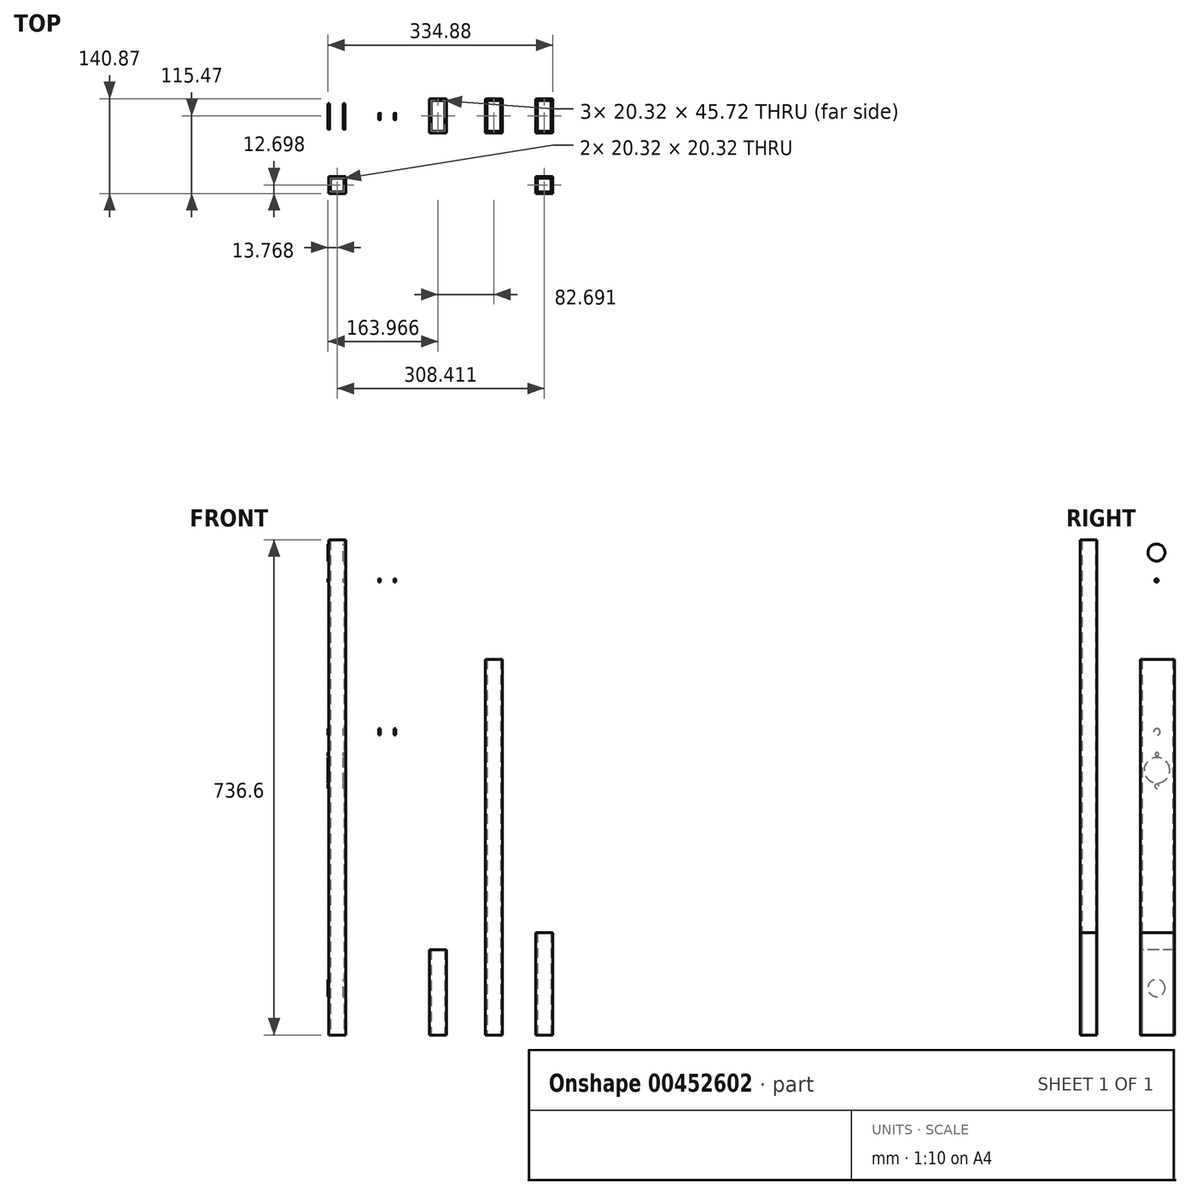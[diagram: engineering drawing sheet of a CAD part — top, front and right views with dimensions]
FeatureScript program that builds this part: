
annotation { "Feature Type Name" : "Feature", "Feature Type Description" : "" }
export const myFeature = defineFeature(function(context is Context, id is Id, definition is map)
    precondition{}
    {
        {
            var Q0;
            Q0=qCreatedBy(makeId("Top.planeOp"),FACE);
            var sketch = newSketch(context, id + "F0", { "sketchPlane" : qUnion([Q0])});
            skLineSegment(sketch, "E0.bottom", {"start": v(-12.7, 25.4) * mm, "end": v(12.7, 25.4) * mm});
            skLineSegment(sketch, "E0.top", {"start": v(-12.7, -25.4) * mm, "end": v(12.7, -25.4) * mm});
            skLineSegment(sketch, "E0.left", {"start": v(-12.7, 25.4) * mm, "end": v(-12.7, -25.4) * mm});
            skLineSegment(sketch, "E0.right", {"start": v(12.7, 25.4) * mm, "end": v(12.7, -25.4) * mm});
            skPoint(sketch, "E0.middle", {"position": v(0, 0) * mm});
            skLineSegment(sketch, "E1.0", {"start": v(-10.16, 22.86) * mm, "end": v(10.16, 22.86) * mm});
            skLineSegment(sketch, "E1.1", {"start": v(-10.16, 22.86) * mm, "end": v(-10.16, -22.86) * mm});
            skLineSegment(sketch, "E1.2", {"start": v(-10.16, -22.86) * mm, "end": v(10.16, -22.86) * mm});
            skLineSegment(sketch, "E1.3", {"start": v(10.16, 22.86) * mm, "end": v(10.16, -22.86) * mm});
            skLineSegment(sketch, "E2", {"start": v(37.87, 30.47) * mm, "end": v(37.87, -46.83) * mm, "construction": true});
            skLineSegment(sketch, "E3.MirrorCS", {"start": v(88.45, 25.4) * mm, "end": v(63.05, 25.4) * mm});
            skLineSegment(sketch, "E4.MirrorCS", {"start": v(88.45, -25.4) * mm, "end": v(63.05, -25.4) * mm});
            skLineSegment(sketch, "E5.MirrorCS", {"start": v(88.45, 25.4) * mm, "end": v(88.45, -25.4) * mm});
            skLineSegment(sketch, "E6.MirrorCS", {"start": v(63.05, 25.4) * mm, "end": v(63.05, -25.4) * mm});
            skPoint(sketch, "E7.MirrorP", {"position": v(75.75, 0) * mm});
            skLineSegment(sketch, "E8.MirrorCS", {"start": v(85.9, 22.86) * mm, "end": v(65.59, 22.86) * mm});
            skLineSegment(sketch, "E9.MirrorCS", {"start": v(85.9, 22.86) * mm, "end": v(85.9, -22.86) * mm});
            skLineSegment(sketch, "E10.MirrorCS", {"start": v(85.9, -22.86) * mm, "end": v(65.59, -22.86) * mm});
            skLineSegment(sketch, "E11.MirrorCS", {"start": v(65.59, 22.86) * mm, "end": v(65.59, -22.86) * mm});
            skLineSegment(sketch, "E12", {"start": v(113.5, 33.8) * mm, "end": v(113.5, -57.25) * mm, "construction": true});
            skPoint(sketch, "E13.MirrorP", {"position": v(151.27, 0) * mm});
            skLineSegment(sketch, "E14.MirrorCS", {"start": v(161.43, 22.86) * mm, "end": v(161.43, -22.86) * mm});
            skLineSegment(sketch, "E15.MirrorCS", {"start": v(163.97, 25.4) * mm, "end": v(163.97, -25.4) * mm});
            skLineSegment(sketch, "E16.MirrorCS", {"start": v(138.57, 25.4) * mm, "end": v(138.57, -25.4) * mm});
            skLineSegment(sketch, "E17.MirrorCS", {"start": v(138.57, -25.4) * mm, "end": v(163.97, -25.4) * mm});
            skLineSegment(sketch, "E18.MirrorCS", {"start": v(138.57, 25.4) * mm, "end": v(163.97, 25.4) * mm});
            skLineSegment(sketch, "E19.MirrorCS", {"start": v(141.1, 22.86) * mm, "end": v(161.43, 22.86) * mm});
            skLineSegment(sketch, "E20.MirrorCS", {"start": v(141.1, -22.86) * mm, "end": v(161.43, -22.86) * mm});
            skLineSegment(sketch, "E21.MirrorCS", {"start": v(141.1, 22.86) * mm, "end": v(141.1, -22.86) * mm});
            skLineSegment(sketch, "E22", {"start": v(192.61, 38.44) * mm, "end": v(192.61, -69.07) * mm, "construction": true});
            skLineSegment(sketch, "E23.MirrorCS", {"start": v(397.93, 25.4) * mm, "end": v(372.53, 25.4) * mm});
            skLineSegment(sketch, "E24.MirrorCS", {"start": v(397.93, -25.4) * mm, "end": v(372.53, -25.4) * mm});
            skLineSegment(sketch, "E25.MirrorCS", {"start": v(395.39, 22.86) * mm, "end": v(375.07, 22.86) * mm});
            skLineSegment(sketch, "E26.MirrorCS", {"start": v(395.39, -22.86) * mm, "end": v(375.07, -22.86) * mm});
            skLineSegment(sketch, "E27.MirrorCS", {"start": v(397.93, 25.4) * mm, "end": v(397.93, -25.4) * mm});
            skLineSegment(sketch, "E28.MirrorCS", {"start": v(395.39, 22.86) * mm, "end": v(395.39, -22.86) * mm});
            skLineSegment(sketch, "E29.MirrorCS", {"start": v(375.07, 22.86) * mm, "end": v(375.07, -22.86) * mm});
            skLineSegment(sketch, "E30.MirrorCS", {"start": v(299.32, 22.86) * mm, "end": v(319.64, 22.86) * mm});
            skLineSegment(sketch, "E31.MirrorCS", {"start": v(299.32, -22.86) * mm, "end": v(319.64, -22.86) * mm});
            skLineSegment(sketch, "E32.MirrorCS", {"start": v(246.66, 25.4) * mm, "end": v(246.66, -25.4) * mm});
            skLineSegment(sketch, "E33.MirrorCS", {"start": v(244.12, 22.86) * mm, "end": v(223.8, 22.86) * mm});
            skLineSegment(sketch, "E34.MirrorCS", {"start": v(244.12, -22.86) * mm, "end": v(223.8, -22.86) * mm});
            skLineSegment(sketch, "E35.MirrorCS", {"start": v(246.66, 25.4) * mm, "end": v(221.26, 25.4) * mm});
            skLineSegment(sketch, "E36.MirrorCS", {"start": v(296.78, 25.4) * mm, "end": v(322.18, 25.4) * mm});
            skLineSegment(sketch, "E37.MirrorCS", {"start": v(296.78, -25.4) * mm, "end": v(322.18, -25.4) * mm});
            skLineSegment(sketch, "E38.MirrorCS", {"start": v(246.66, -25.4) * mm, "end": v(221.26, -25.4) * mm});
            skLineSegment(sketch, "E39.MirrorCS", {"start": v(223.8, 22.86) * mm, "end": v(223.8, -22.86) * mm});
            skLineSegment(sketch, "E40.MirrorCS", {"start": v(299.32, 22.86) * mm, "end": v(299.32, -22.86) * mm});
            skLineSegment(sketch, "E41.MirrorCS", {"start": v(319.64, 22.86) * mm, "end": v(319.64, -22.86) * mm});
            skLineSegment(sketch, "E42.MirrorCS", {"start": v(372.53, 25.4) * mm, "end": v(372.53, -25.4) * mm});
            skPoint(sketch, "E43.MirrorP", {"position": v(385.23, 0) * mm});
            skLineSegment(sketch, "E44.MirrorCS", {"start": v(244.12, 22.86) * mm, "end": v(244.12, -22.86) * mm});
            skLineSegment(sketch, "E45.MirrorCS", {"start": v(221.26, 25.4) * mm, "end": v(221.26, -25.4) * mm});
            skLineSegment(sketch, "E46.MirrorCS", {"start": v(296.78, 25.4) * mm, "end": v(296.78, -25.4) * mm});
            skPoint(sketch, "E47.MirrorP", {"position": v(233.96, 0) * mm});
            skPoint(sketch, "E48.MirrorP", {"position": v(309.48, 0) * mm});
            skLineSegment(sketch, "E49.MirrorCS", {"start": v(271.72, 33.8) * mm, "end": v(271.72, -57.25) * mm, "construction": true});
            skLineSegment(sketch, "E50.MirrorCS", {"start": v(347.35, 30.47) * mm, "end": v(347.35, -46.83) * mm, "construction": true});
            skLineSegment(sketch, "E51.MirrorCS", {"start": v(322.18, 25.4) * mm, "end": v(322.18, -25.4) * mm});
            skLineSegment(sketch, "E52", {"start": v(-40.7, 40.51) * mm, "end": v(-40.7, -117.08) * mm, "construction": true});
            skLineSegment(sketch, "E53.MirrorCS", {"start": v(-479.32, 25.4) * mm, "end": v(-453.92, 25.4) * mm});
            skLineSegment(sketch, "E54.MirrorCS", {"start": v(-476.78, 22.86) * mm, "end": v(-456.46, 22.86) * mm});
            skLineSegment(sketch, "E55.MirrorCS", {"start": v(-479.32, -25.4) * mm, "end": v(-453.92, -25.4) * mm});
            skLineSegment(sketch, "E56.MirrorCS", {"start": v(-68.7, -25.4) * mm, "end": v(-94.1, -25.4) * mm});
            skLineSegment(sketch, "E57.MirrorCS", {"start": v(-453.92, 25.4) * mm, "end": v(-453.92, -25.4) * mm});
            skLineSegment(sketch, "E58.MirrorCS", {"start": v(-68.7, 25.4) * mm, "end": v(-94.1, 25.4) * mm});
            skLineSegment(sketch, "E59.MirrorCS", {"start": v(-71.23, -22.86) * mm, "end": v(-91.55, -22.86) * mm});
            skLineSegment(sketch, "E60.MirrorCS", {"start": v(-476.78, -22.86) * mm, "end": v(-456.46, -22.86) * mm});
            skLineSegment(sketch, "E61.MirrorCS", {"start": v(-71.23, 22.86) * mm, "end": v(-91.55, 22.86) * mm});
            skLineSegment(sketch, "E62.MirrorCS", {"start": v(-456.46, 22.86) * mm, "end": v(-456.46, -22.86) * mm});
            skLineSegment(sketch, "E63.MirrorCS", {"start": v(-68.7, 25.4) * mm, "end": v(-68.7, -25.4) * mm});
            skLineSegment(sketch, "E64.MirrorCS", {"start": v(-479.32, 25.4) * mm, "end": v(-479.32, -25.4) * mm});
            skLineSegment(sketch, "E65.MirrorCS", {"start": v(-328.05, 25.4) * mm, "end": v(-302.65, 25.4) * mm});
            skLineSegment(sketch, "E66.MirrorCS", {"start": v(-476.78, 22.86) * mm, "end": v(-476.78, -22.86) * mm});
            skLineSegment(sketch, "E67.MirrorCS", {"start": v(-219.96, 25.4) * mm, "end": v(-245.36, 25.4) * mm});
            skLineSegment(sketch, "E68.MirrorCS", {"start": v(-325.51, 22.86) * mm, "end": v(-305.2, 22.86) * mm});
            skLineSegment(sketch, "E69.MirrorCS", {"start": v(-222.5, 22.86) * mm, "end": v(-242.82, 22.86) * mm});
            skLineSegment(sketch, "E70.MirrorCS", {"start": v(-91.55, 22.86) * mm, "end": v(-91.55, -22.86) * mm});
            skLineSegment(sketch, "E71.MirrorCS", {"start": v(-71.23, 22.86) * mm, "end": v(-71.23, -22.86) * mm});
            skLineSegment(sketch, "E72.MirrorCS", {"start": v(-325.51, -22.86) * mm, "end": v(-305.2, -22.86) * mm});
            skLineSegment(sketch, "E73.MirrorCS", {"start": v(-219.96, -25.4) * mm, "end": v(-245.36, -25.4) * mm});
            skLineSegment(sketch, "E74.MirrorCS", {"start": v(-380.71, 22.86) * mm, "end": v(-401.03, 22.86) * mm});
            skLineSegment(sketch, "E75.MirrorCS", {"start": v(-380.71, -22.86) * mm, "end": v(-401.03, -22.86) * mm});
            skLineSegment(sketch, "E76.MirrorCS", {"start": v(-378.17, 25.4) * mm, "end": v(-403.57, 25.4) * mm});
            skLineSegment(sketch, "E77.MirrorCS", {"start": v(-167.3, 22.86) * mm, "end": v(-146.98, 22.86) * mm});
            skLineSegment(sketch, "E78.MirrorCS", {"start": v(-167.3, -22.86) * mm, "end": v(-146.98, -22.86) * mm});
            skLineSegment(sketch, "E79.MirrorCS", {"start": v(-378.17, -25.4) * mm, "end": v(-403.57, -25.4) * mm});
            skLineSegment(sketch, "E80.MirrorCS", {"start": v(-169.84, 25.4) * mm, "end": v(-144.44, 25.4) * mm});
            skLineSegment(sketch, "E81.MirrorCS", {"start": v(-169.84, -25.4) * mm, "end": v(-144.44, -25.4) * mm});
            skLineSegment(sketch, "E82.MirrorCS", {"start": v(-222.5, -22.86) * mm, "end": v(-242.82, -22.86) * mm});
            skLineSegment(sketch, "E83.MirrorCS", {"start": v(-328.05, -25.4) * mm, "end": v(-302.65, -25.4) * mm});
            skPoint(sketch, "E84.MirrorP", {"position": v(-466.62, 0) * mm});
            skLineSegment(sketch, "E85.MirrorCS", {"start": v(-305.2, 22.86) * mm, "end": v(-305.2, -22.86) * mm});
            skLineSegment(sketch, "E86.MirrorCS", {"start": v(-242.82, 22.86) * mm, "end": v(-242.82, -22.86) * mm});
            skLineSegment(sketch, "E87.MirrorCS", {"start": v(-380.71, 22.86) * mm, "end": v(-380.71, -22.86) * mm});
            skLineSegment(sketch, "E88.MirrorCS", {"start": v(-245.36, 25.4) * mm, "end": v(-245.36, -25.4) * mm});
            skLineSegment(sketch, "E89.MirrorCS", {"start": v(-403.57, 25.4) * mm, "end": v(-403.57, -25.4) * mm});
            skPoint(sketch, "E90.MirrorP", {"position": v(-81.4, 0) * mm});
            skLineSegment(sketch, "E91.MirrorCS", {"start": v(-401.03, 22.86) * mm, "end": v(-401.03, -22.86) * mm});
            skLineSegment(sketch, "E92.MirrorCS", {"start": v(-325.51, 22.86) * mm, "end": v(-325.51, -22.86) * mm});
            skLineSegment(sketch, "E93.MirrorCS", {"start": v(-167.3, 22.86) * mm, "end": v(-167.3, -22.86) * mm});
            skLineSegment(sketch, "E94.MirrorCS", {"start": v(-144.44, 25.4) * mm, "end": v(-144.44, -25.4) * mm});
            skLineSegment(sketch, "E95.MirrorCS", {"start": v(-222.5, 22.86) * mm, "end": v(-222.5, -22.86) * mm});
            skLineSegment(sketch, "E96.MirrorCS", {"start": v(-328.05, 25.4) * mm, "end": v(-328.05, -25.4) * mm});
            skLineSegment(sketch, "E97.MirrorCS", {"start": v(-146.98, 22.86) * mm, "end": v(-146.98, -22.86) * mm});
            skLineSegment(sketch, "E98.MirrorCS", {"start": v(-94.1, 25.4) * mm, "end": v(-94.1, -25.4) * mm});
            skLineSegment(sketch, "E99.MirrorCS", {"start": v(-274, 38.44) * mm, "end": v(-274, -69.07) * mm, "construction": true});
            skLineSegment(sketch, "E100.MirrorCS", {"start": v(-428.75, 30.47) * mm, "end": v(-428.75, -46.83) * mm, "construction": true});
            skPoint(sketch, "E101.MirrorP", {"position": v(-157.14, 0) * mm});
            skLineSegment(sketch, "E102.MirrorCS", {"start": v(-219.96, 25.4) * mm, "end": v(-219.96, -25.4) * mm});
            skPoint(sketch, "E103.MirrorP", {"position": v(-232.66, 0) * mm});
            skLineSegment(sketch, "E104.MirrorCS", {"start": v(-302.65, 25.4) * mm, "end": v(-302.65, -25.4) * mm});
            skLineSegment(sketch, "E105.MirrorCS", {"start": v(-119.27, 30.47) * mm, "end": v(-119.27, -46.83) * mm, "construction": true});
            skLineSegment(sketch, "E106.MirrorCS", {"start": v(-194.9, 33.8) * mm, "end": v(-194.9, -57.25) * mm, "construction": true});
            skLineSegment(sketch, "E107.MirrorCS", {"start": v(-353.11, 33.8) * mm, "end": v(-353.11, -57.25) * mm, "construction": true});
            skPoint(sketch, "E108.MirrorP", {"position": v(-390.87, 0) * mm});
            skLineSegment(sketch, "E109.MirrorCS", {"start": v(-378.17, 25.4) * mm, "end": v(-378.17, -25.4) * mm});
            skLineSegment(sketch, "E110.MirrorCS", {"start": v(-169.84, 25.4) * mm, "end": v(-169.84, -25.4) * mm});
            skPoint(sketch, "E111.MirrorP", {"position": v(-315.35, 0) * mm});
            skSolve(sketch);
        }
        {
            var Q0;
            Q0=makeQuery(id+"F0.imprint","IMPRINT",FACE,{"disambiguationData":[TD([[makeQuery(id+"F0.imprint","IMPRINT",EDGE,{"derivedFrom":sQuery(id+"F0.wireOp",EDGE,"E54.MirrorCS")}),1.0]])]});
            extrude(context, id + "F1", {"entities" : qUnion([Q0]), "depth" : 736.6 * mm});
        }
        {
            var Q0;
            Q0=makeQuery(id+"F0.imprint","IMPRINT",FACE,{"disambiguationData":[TD([[makeQuery(id+"F0.imprint","IMPRINT",EDGE,{"derivedFrom":sQuery(id+"F0.wireOp",EDGE,"E74.MirrorCS")}),-1.0]])]});
            extrude(context, id + "F2", {"entities" : qUnion([Q0]), "depth" : 787.4 * mm});
        }
        {
            var Q0;
            Q0=makeQuery(id+"F0.imprint","IMPRINT",FACE,{"disambiguationData":[TD([[makeQuery(id+"F0.imprint","IMPRINT",EDGE,{"derivedFrom":sQuery(id+"F0.wireOp",EDGE,"E65.MirrorCS")}),-1.0]])]});
            extrude(context, id + "F3", {"entities" : qUnion([Q0]), "depth" : 127 * mm});
        }
        {
            var Q0;
            Q0=makeQuery(id+"F0.imprint","IMPRINT",FACE,{"disambiguationData":[TD([[makeQuery(id+"F0.imprint","IMPRINT",EDGE,{"derivedFrom":sQuery(id+"F0.wireOp",EDGE,"E67.MirrorCS")}),1.0]])]});
            extrude(context, id + "F4", {"entities" : qUnion([Q0]), "depth" : 558.8 * mm});
        }
        {
            var Q0;
            Q0=makeQuery(id+"F2.opExtrude","SWEPT_FACE",FACE,{"disambiguationData":[OSD([sQuery(id+"F0.wireOp",EDGE,"E109.MirrorCS")])]});
            var sketch = newSketch(context, id + "F5", { "sketchPlane" : qUnion([Q0])});
            skPoint(sketch, "E112.centerSnap0", {"position": v(-25.4, 393.7) * mm});
            skPoint(sketch, "E113.positionSnap0", {"position": v(25.4, 393.7) * mm});
            skPoint(sketch, "E114", {"position": v(-0.95, 393.7) * mm});
            skPoint(sketch, "E115.visualSharp", {"position": v(16.51, 376.24) * mm});
            skPoint(sketch, "E116.visualSharp", {"position": v(-18.41, 411.16) * mm});
            skPoint(sketch, "E117.visualSharp", {"position": v(-18.41, 376.24) * mm});
            skPoint(sketch, "E118.visualSharp", {"position": v(16.51, 411.16) * mm});
            skCircle(sketch, "E119", {"center": v(-0.95, 393.7) * mm, "radius": 23.81 * mm, "construction": true});
            skCircle(sketch, "E120", {"center": v(-0.95, 369.89) * mm, "radius": 3.06 * mm});
            skPoint(sketch, "E120.centerSnap0", {"position": v(-0.95, 376.24) * mm});
            skCircle(sketch, "E121", {"center": v(-0.95, 417.51) * mm, "radius": 2.55 * mm});
            skPoint(sketch, "E121.centerSnap0", {"position": v(-0.95, 411.16) * mm});
            skPoint(sketch, "E122", {"position": v(-1.59, 69.85) * mm});
            skCircle(sketch, "E123", {"center": v(-1.59, 69.85) * mm, "radius": 12.7 * mm});
            skPoint(sketch, "E124", {"position": v(-1.59, 717.55) * mm});
            skCircle(sketch, "E125", {"center": v(-1.59, 717.55) * mm, "radius": 12.7 * mm});
            skCircle(sketch, "E126", {"center": v(-0.95, 393.7) * mm, "radius": 19.05 * mm});
            skCircle(sketch, "E127", {"center": v(-1.59, 111.5) * mm, "radius": 2.55 * mm});
            skLineSegment(sketch, "E128", {"start": v(83.7, 393.7) * mm, "end": v(-46.1, 393.7) * mm, "construction": true});
            skCircle(sketch, "E129.MirrorC", {"center": v(-1.59, 675.9) * mm, "radius": 2.55 * mm});
            skCircle(sketch, "E130", {"center": v(-0.95, 336.55) * mm, "radius": 4.76 * mm});
            skCircle(sketch, "E131.MirrorC", {"center": v(-0.95, 450.85) * mm, "radius": 4.76 * mm, "construction": true});
            skCircle(sketch, "E132.MirrorC", {"center": v(-0.95, 450.85) * mm, "radius": 4.76 * mm});
            skSolve(sketch);
        }
        {
            var Q0;
            Q0=makeQuery(id+"F5.imprint","IMPRINT",FACE,{"disambiguationData":[TD([[makeQuery(id+"F5.imprint","IMPRINT",EDGE,{"derivedFrom":sQuery(id+"F5.wireOp",EDGE,"E120")}),1.0]])]});
            var Q1;
            Q1=makeQuery(id+"F5.imprint","IMPRINT",FACE,{"disambiguationData":[TD([[makeQuery(id+"F5.imprint","IMPRINT",EDGE,{"derivedFrom":sQuery(id+"F5.wireOp",EDGE,"E121")}),1.0]])]});
            extrude(context, id + "F6", {"entities" : qUnion([Q0, Q1]), "operationType" : NewBodyOperationType.REMOVE, "oppositeDirection" : true, "depth" : 25.4 * mm});
        }
        {
            var Q0;
            Q0=makeQuery(id+"F5.imprint","IMPRINT",FACE,{"disambiguationData":[TD([[makeQuery(id+"F5.imprint","IMPRINT",EDGE,{"derivedFrom":sQuery(id+"F5.wireOp",EDGE,"E125")}),1.0]])]});
            extrude(context, id + "F7", {"entities" : qUnion([Q0]), "operationType" : NewBodyOperationType.REMOVE, "oppositeDirection" : true, "depth" : 25.4 * mm});
        }
        {
            var Q0;
            Q0=makeQuery(id+"F5.imprint","IMPRINT",FACE,{"disambiguationData":[TD([[makeQuery(id+"F5.imprint","IMPRINT",EDGE,{"derivedFrom":sQuery(id+"F5.wireOp",EDGE,"E123")}),1.0]])]});
            extrude(context, id + "F8", {"entities" : qUnion([Q0]), "operationType" : NewBodyOperationType.REMOVE, "oppositeDirection" : true, "depth" : 25.4 * mm});
        }
        {
            var Q0;
            Q0=makeQuery(id+"F0.imprint","IMPRINT",FACE,{"disambiguationData":[TD([[makeQuery(id+"F0.imprint","IMPRINT",EDGE,{"derivedFrom":sQuery(id+"F0.wireOp",EDGE,"E77.MirrorCS")}),1.0]])]});
            extrude(context, id + "F9", {"entities" : qUnion([Q0]), "depth" : 152.4 * mm});
        }
        {
            var Q0;
            Q0=qCreatedBy(makeId("Top.planeOp"),FACE);
            var sketch = newSketch(context, id + "F10", { "sketchPlane" : qUnion([Q0])});
            skLineSegment(sketch, "E133.bottom", {"start": v(12.7, -90.07) * mm, "end": v(-12.7, -90.07) * mm});
            skLineSegment(sketch, "E133.top", {"start": v(12.7, -115.47) * mm, "end": v(-12.7, -115.47) * mm});
            skLineSegment(sketch, "E133.left", {"start": v(12.7, -90.07) * mm, "end": v(12.7, -115.47) * mm});
            skLineSegment(sketch, "E133.right", {"start": v(-12.7, -90.07) * mm, "end": v(-12.7, -115.47) * mm});
            skPoint(sketch, "E133.middle", {"position": v(0, -102.77) * mm});
            skLineSegment(sketch, "E134.0", {"start": v(10.16, -92.61) * mm, "end": v(10.16, -112.93) * mm});
            skLineSegment(sketch, "E134.1", {"start": v(10.16, -92.61) * mm, "end": v(-10.16, -92.61) * mm});
            skLineSegment(sketch, "E134.2", {"start": v(-10.16, -92.61) * mm, "end": v(-10.16, -112.93) * mm});
            skLineSegment(sketch, "E134.3", {"start": v(10.16, -112.93) * mm, "end": v(-10.16, -112.93) * mm});
            skLineSegment(sketch, "E135.MirrorCS", {"start": v(-94.1, -90.07) * mm, "end": v(-68.7, -90.07) * mm});
            skLineSegment(sketch, "E136.MirrorCS", {"start": v(-91.55, -92.61) * mm, "end": v(-91.55, -112.93) * mm});
            skLineSegment(sketch, "E137.MirrorCS", {"start": v(-68.7, -90.07) * mm, "end": v(-68.7, -115.47) * mm});
            skLineSegment(sketch, "E138.MirrorCS", {"start": v(-94.1, -90.07) * mm, "end": v(-94.1, -115.47) * mm});
            skLineSegment(sketch, "E139.MirrorCS", {"start": v(-91.55, -112.93) * mm, "end": v(-71.23, -112.93) * mm});
            skLineSegment(sketch, "E140.MirrorCS", {"start": v(-71.23, -92.61) * mm, "end": v(-71.23, -112.93) * mm});
            skLineSegment(sketch, "E141.MirrorCS", {"start": v(-94.1, -115.47) * mm, "end": v(-68.7, -115.47) * mm});
            skPoint(sketch, "E142.MirrorP", {"position": v(-81.4, -102.77) * mm});
            skLineSegment(sketch, "E143.MirrorCS", {"start": v(-91.55, -92.61) * mm, "end": v(-71.23, -92.61) * mm});
            skLineSegment(sketch, "E144.MirrorCS", {"start": v(216.86, -112.93) * mm, "end": v(237.18, -112.93) * mm});
            skLineSegment(sketch, "E145.MirrorCS", {"start": v(318.57, -92.61) * mm, "end": v(318.57, -112.93) * mm});
            skLineSegment(sketch, "E146.MirrorCS", {"start": v(321.11, -90.07) * mm, "end": v(321.11, -115.47) * mm});
            skLineSegment(sketch, "E147.MirrorCS", {"start": v(321.11, -115.47) * mm, "end": v(295.71, -115.47) * mm});
            skLineSegment(sketch, "E148.MirrorCS", {"start": v(214.32, -115.47) * mm, "end": v(239.72, -115.47) * mm});
            skLineSegment(sketch, "E149.MirrorCS", {"start": v(239.72, -90.07) * mm, "end": v(239.72, -115.47) * mm});
            skLineSegment(sketch, "E150.MirrorCS", {"start": v(216.86, -92.61) * mm, "end": v(237.18, -92.61) * mm});
            skPoint(sketch, "E151.MirrorP", {"position": v(227.02, -102.77) * mm});
            skPoint(sketch, "E152.MirrorP", {"position": v(308.41, -102.77) * mm});
            skLineSegment(sketch, "E153.MirrorCS", {"start": v(295.71, -90.07) * mm, "end": v(295.71, -115.47) * mm});
            skLineSegment(sketch, "E154.MirrorCS", {"start": v(321.11, -90.07) * mm, "end": v(295.71, -90.07) * mm});
            skLineSegment(sketch, "E155.MirrorCS", {"start": v(318.57, -92.61) * mm, "end": v(298.25, -92.61) * mm});
            skLineSegment(sketch, "E156.MirrorCS", {"start": v(298.25, -92.61) * mm, "end": v(298.25, -112.93) * mm});
            skLineSegment(sketch, "E157.MirrorCS", {"start": v(318.57, -112.93) * mm, "end": v(298.25, -112.93) * mm});
            skLineSegment(sketch, "E158.MirrorCS", {"start": v(214.32, -90.07) * mm, "end": v(239.72, -90.07) * mm});
            skLineSegment(sketch, "E159.MirrorCS", {"start": v(216.86, -92.61) * mm, "end": v(216.86, -112.93) * mm});
            skLineSegment(sketch, "E160.MirrorCS", {"start": v(214.32, -90.07) * mm, "end": v(214.32, -115.47) * mm});
            skLineSegment(sketch, "E161.MirrorCS", {"start": v(237.18, -92.61) * mm, "end": v(237.18, -112.93) * mm});
            skLineSegment(sketch, "E162.MirrorCS", {"start": v(65.59, -112.93) * mm, "end": v(85.9, -112.93) * mm});
            skLineSegment(sketch, "E163.MirrorCS", {"start": v(65.59, -92.61) * mm, "end": v(65.59, -112.93) * mm});
            skPoint(sketch, "E164.MirrorP", {"position": v(75.75, -102.77) * mm});
            skLineSegment(sketch, "E165.MirrorCS", {"start": v(88.45, -90.07) * mm, "end": v(88.45, -115.47) * mm});
            skLineSegment(sketch, "E166.MirrorCS", {"start": v(63.05, -90.07) * mm, "end": v(63.05, -115.47) * mm});
            skLineSegment(sketch, "E167.MirrorCS", {"start": v(63.05, -115.47) * mm, "end": v(88.45, -115.47) * mm});
            skLineSegment(sketch, "E168.MirrorCS", {"start": v(63.05, -90.07) * mm, "end": v(88.45, -90.07) * mm});
            skLineSegment(sketch, "E169.MirrorCS", {"start": v(85.9, -92.61) * mm, "end": v(85.9, -112.93) * mm});
            skLineSegment(sketch, "E170.MirrorCS", {"start": v(65.59, -92.61) * mm, "end": v(85.9, -92.61) * mm});
            skLineSegment(sketch, "E171.MirrorCS", {"start": v(161.43, -92.61) * mm, "end": v(161.43, -112.93) * mm});
            skLineSegment(sketch, "E172.MirrorCS", {"start": v(163.97, -90.07) * mm, "end": v(138.57, -90.07) * mm});
            skLineSegment(sketch, "E173.MirrorCS", {"start": v(141.1, -92.61) * mm, "end": v(141.1, -112.93) * mm});
            skLineSegment(sketch, "E174.MirrorCS", {"start": v(138.57, -90.07) * mm, "end": v(138.57, -115.47) * mm});
            skPoint(sketch, "E175.MirrorP", {"position": v(151.27, -102.77) * mm});
            skLineSegment(sketch, "E176.MirrorCS", {"start": v(163.97, -90.07) * mm, "end": v(163.97, -115.47) * mm});
            skLineSegment(sketch, "E177.MirrorCS", {"start": v(163.97, -115.47) * mm, "end": v(138.57, -115.47) * mm});
            skLineSegment(sketch, "E178.MirrorCS", {"start": v(161.43, -112.93) * mm, "end": v(141.1, -112.93) * mm});
            skLineSegment(sketch, "E179.MirrorCS", {"start": v(161.43, -92.61) * mm, "end": v(141.1, -92.61) * mm});
            skLineSegment(sketch, "E180.MirrorCS", {"start": v(373.6, -115.47) * mm, "end": v(399, -115.47) * mm});
            skLineSegment(sketch, "E181.MirrorCS", {"start": v(396.46, -92.61) * mm, "end": v(396.46, -112.93) * mm});
            skLineSegment(sketch, "E182.MirrorCS", {"start": v(376.14, -112.93) * mm, "end": v(396.46, -112.93) * mm});
            skLineSegment(sketch, "E183.MirrorCS", {"start": v(399, -90.07) * mm, "end": v(399, -115.47) * mm});
            skPoint(sketch, "E184.MirrorP", {"position": v(386.3, -102.77) * mm});
            skLineSegment(sketch, "E185.MirrorCS", {"start": v(373.6, -90.07) * mm, "end": v(399, -90.07) * mm});
            skLineSegment(sketch, "E186.MirrorCS", {"start": v(376.14, -92.61) * mm, "end": v(376.14, -112.93) * mm});
            skLineSegment(sketch, "E187.MirrorCS", {"start": v(373.6, -90.07) * mm, "end": v(373.6, -115.47) * mm});
            skLineSegment(sketch, "E188.MirrorCS", {"start": v(376.14, -92.61) * mm, "end": v(396.46, -92.61) * mm});
            skPoint(sketch, "E189.MirrorP", {"position": v(-157.14, -102.77) * mm});
            skLineSegment(sketch, "E190.MirrorCS", {"start": v(-248.7, -112.93) * mm, "end": v(-228.38, -112.93) * mm});
            skLineSegment(sketch, "E191.MirrorCS", {"start": v(-304.12, -92.61) * mm, "end": v(-304.12, -112.93) * mm});
            skLineSegment(sketch, "E192.MirrorCS", {"start": v(-251.24, -90.07) * mm, "end": v(-251.24, -115.47) * mm});
            skLineSegment(sketch, "E193.MirrorCS", {"start": v(-452.85, -90.07) * mm, "end": v(-452.85, -115.47) * mm});
            skLineSegment(sketch, "E194.MirrorCS", {"start": v(-379.64, -92.61) * mm, "end": v(-379.64, -112.93) * mm});
            skLineSegment(sketch, "E195.MirrorCS", {"start": v(-455.4, -92.61) * mm, "end": v(-475.71, -92.61) * mm});
            skLineSegment(sketch, "E196.MirrorCS", {"start": v(-399.96, -112.93) * mm, "end": v(-379.64, -112.93) * mm});
            skLineSegment(sketch, "E197.MirrorCS", {"start": v(-144.44, -90.07) * mm, "end": v(-169.84, -90.07) * mm});
            skLineSegment(sketch, "E198.MirrorCS", {"start": v(-167.3, -92.61) * mm, "end": v(-167.3, -112.93) * mm});
            skLineSegment(sketch, "E199.MirrorCS", {"start": v(-324.44, -92.61) * mm, "end": v(-324.44, -112.93) * mm});
            skLineSegment(sketch, "E200.MirrorCS", {"start": v(-225.84, -90.07) * mm, "end": v(-225.84, -115.47) * mm});
            skLineSegment(sketch, "E201.MirrorCS", {"start": v(-304.12, -92.61) * mm, "end": v(-324.44, -92.61) * mm});
            skLineSegment(sketch, "E202.MirrorCS", {"start": v(-146.98, -92.61) * mm, "end": v(-146.98, -112.93) * mm});
            skLineSegment(sketch, "E203.MirrorCS", {"start": v(-452.85, -90.07) * mm, "end": v(-478.25, -90.07) * mm});
            skLineSegment(sketch, "E204.MirrorCS", {"start": v(-301.58, -90.07) * mm, "end": v(-301.58, -115.47) * mm});
            skLineSegment(sketch, "E205.MirrorCS", {"start": v(-144.44, -115.47) * mm, "end": v(-169.84, -115.47) * mm});
            skLineSegment(sketch, "E206.MirrorCS", {"start": v(-248.7, -92.61) * mm, "end": v(-248.7, -112.93) * mm});
            skPoint(sketch, "E207.MirrorP", {"position": v(-238.54, -102.77) * mm});
            skLineSegment(sketch, "E208.MirrorCS", {"start": v(-455.4, -112.93) * mm, "end": v(-475.71, -112.93) * mm});
            skLineSegment(sketch, "E209.MirrorCS", {"start": v(-402.5, -90.07) * mm, "end": v(-402.5, -115.47) * mm});
            skLineSegment(sketch, "E210.MirrorCS", {"start": v(-304.12, -112.93) * mm, "end": v(-324.44, -112.93) * mm});
            skLineSegment(sketch, "E211.MirrorCS", {"start": v(-169.84, -90.07) * mm, "end": v(-169.84, -115.47) * mm});
            skLineSegment(sketch, "E212.MirrorCS", {"start": v(-455.4, -92.61) * mm, "end": v(-455.4, -112.93) * mm});
            skLineSegment(sketch, "E213.MirrorCS", {"start": v(-146.98, -92.61) * mm, "end": v(-167.3, -92.61) * mm});
            skLineSegment(sketch, "E214.MirrorCS", {"start": v(-478.25, -90.07) * mm, "end": v(-478.25, -115.47) * mm});
            skPoint(sketch, "E215.MirrorP", {"position": v(-389.8, -102.77) * mm});
            skLineSegment(sketch, "E216.MirrorCS", {"start": v(-402.5, -90.07) * mm, "end": v(-377.1, -90.07) * mm});
            skLineSegment(sketch, "E217.MirrorCS", {"start": v(-248.7, -92.61) * mm, "end": v(-228.38, -92.61) * mm});
            skLineSegment(sketch, "E218.MirrorCS", {"start": v(-402.5, -115.47) * mm, "end": v(-377.1, -115.47) * mm});
            skLineSegment(sketch, "E219.MirrorCS", {"start": v(-301.58, -90.07) * mm, "end": v(-326.98, -90.07) * mm});
            skLineSegment(sketch, "E220.MirrorCS", {"start": v(-144.44, -90.07) * mm, "end": v(-144.44, -115.47) * mm});
            skPoint(sketch, "E221.MirrorP", {"position": v(-465.55, -102.77) * mm});
            skLineSegment(sketch, "E222.MirrorCS", {"start": v(-228.38, -92.61) * mm, "end": v(-228.38, -112.93) * mm});
            skLineSegment(sketch, "E223.MirrorCS", {"start": v(-326.98, -90.07) * mm, "end": v(-326.98, -115.47) * mm});
            skLineSegment(sketch, "E224.MirrorCS", {"start": v(-475.71, -92.61) * mm, "end": v(-475.71, -112.93) * mm});
            skLineSegment(sketch, "E225.MirrorCS", {"start": v(-146.98, -112.93) * mm, "end": v(-167.3, -112.93) * mm});
            skLineSegment(sketch, "E226.MirrorCS", {"start": v(-377.1, -90.07) * mm, "end": v(-377.1, -115.47) * mm});
            skLineSegment(sketch, "E227.MirrorCS", {"start": v(-399.96, -92.61) * mm, "end": v(-379.64, -92.61) * mm});
            skLineSegment(sketch, "E228.MirrorCS", {"start": v(-251.24, -90.07) * mm, "end": v(-225.84, -90.07) * mm});
            skPoint(sketch, "E229.MirrorP", {"position": v(-314.28, -102.77) * mm});
            skLineSegment(sketch, "E230.MirrorCS", {"start": v(-452.85, -115.47) * mm, "end": v(-478.25, -115.47) * mm});
            skLineSegment(sketch, "E231.MirrorCS", {"start": v(-399.96, -92.61) * mm, "end": v(-399.96, -112.93) * mm});
            skLineSegment(sketch, "E232.MirrorCS", {"start": v(-251.24, -115.47) * mm, "end": v(-225.84, -115.47) * mm});
            skLineSegment(sketch, "E233.MirrorCS", {"start": v(-301.58, -115.47) * mm, "end": v(-326.98, -115.47) * mm});
            skSolve(sketch);
        }
        {
            var Q0;
            Q0=makeQuery(id+"F10.imprint","IMPRINT",FACE,{"disambiguationData":[TD([[makeQuery(id+"F10.imprint","IMPRINT",EDGE,{"derivedFrom":sQuery(id+"F10.wireOp",EDGE,"E193.MirrorCS")}),-1.0]])]});
            extrude(context, id + "F11", {"entities" : qUnion([Q0]), "depth" : 736.6 * mm});
        }
        {
            var Q0;
            Q0=makeQuery(id+"F10.imprint","IMPRINT",FACE,{"disambiguationData":[TD([[makeQuery(id+"F10.imprint","IMPRINT",EDGE,{"derivedFrom":sQuery(id+"F10.wireOp",EDGE,"E197.MirrorCS")}),1.0]])]});
            extrude(context, id + "F12", {"entities" : qUnion([Q0]), "depth" : 152.4 * mm});
        }
        {
            var Q0;
            Q0=makeQuery(id+"F5.imprint","IMPRINT",FACE,{"disambiguationData":[TD([[makeQuery(id+"F5.imprint","IMPRINT",EDGE,{"derivedFrom":sQuery(id+"F5.wireOp",EDGE,"E126")}),1.0]])]});
            extrude(context, id + "F13", {"entities" : qUnion([Q0]), "operationType" : NewBodyOperationType.REMOVE, "oppositeDirection" : true, "depth" : 25.4 * mm});
        }
        {
            var Q0;
            Q0=makeQuery(id+"F5.imprint","IMPRINT",FACE,{"disambiguationData":[TD([[makeQuery(id+"F5.imprint","IMPRINT",EDGE,{"derivedFrom":sQuery(id+"F5.wireOp",EDGE,"E127")}),1.0]])]});
            var Q1;
            Q1=sQuery(id+"F5.wireOp",EDGE,"E127");
            extrude(context, id + "F14", {"entities" : qUnion([Q0]), "operationType" : NewBodyOperationType.REMOVE, "surfaceEntities" : qUnion([Q1]), "endBound" : BoundingType.THROUGH_ALL, "oppositeDirection" : true, "depth" : 25.4 * mm});
        }
        {
            var Q0;
            Q0=makeQuery(id+"F5.imprint","IMPRINT",FACE,{"disambiguationData":[TD([[makeQuery(id+"F5.imprint","IMPRINT",EDGE,{"derivedFrom":sQuery(id+"F5.wireOp",EDGE,"E129.MirrorC")}),-1.0]])]});
            extrude(context, id + "F15", {"entities" : qUnion([Q0]), "operationType" : NewBodyOperationType.REMOVE, "oppositeDirection" : true, "depth" : 25.4 * mm});
        }
        {
            var Q0;
            Q0=makeQuery(id+"F5.imprint","IMPRINT",FACE,{"disambiguationData":[TD([[makeQuery(id+"F5.imprint","IMPRINT",EDGE,{"derivedFrom":sQuery(id+"F5.wireOp",EDGE,"E132.MirrorC")}),-1.0]])]});
            var Q1;
            Q1=makeQuery(id+"F5.imprint","IMPRINT",FACE,{"disambiguationData":[TD([[makeQuery(id+"F5.imprint","IMPRINT",EDGE,{"derivedFrom":sQuery(id+"F5.wireOp",EDGE,"E130")}),1.0]])]});
            extrude(context, id + "F16", {"entities" : qUnion([Q0, Q1]), "operationType" : NewBodyOperationType.REMOVE, "endBound" : BoundingType.THROUGH_ALL, "oppositeDirection" : true, "depth" : 25.4 * mm});
        }
    });
